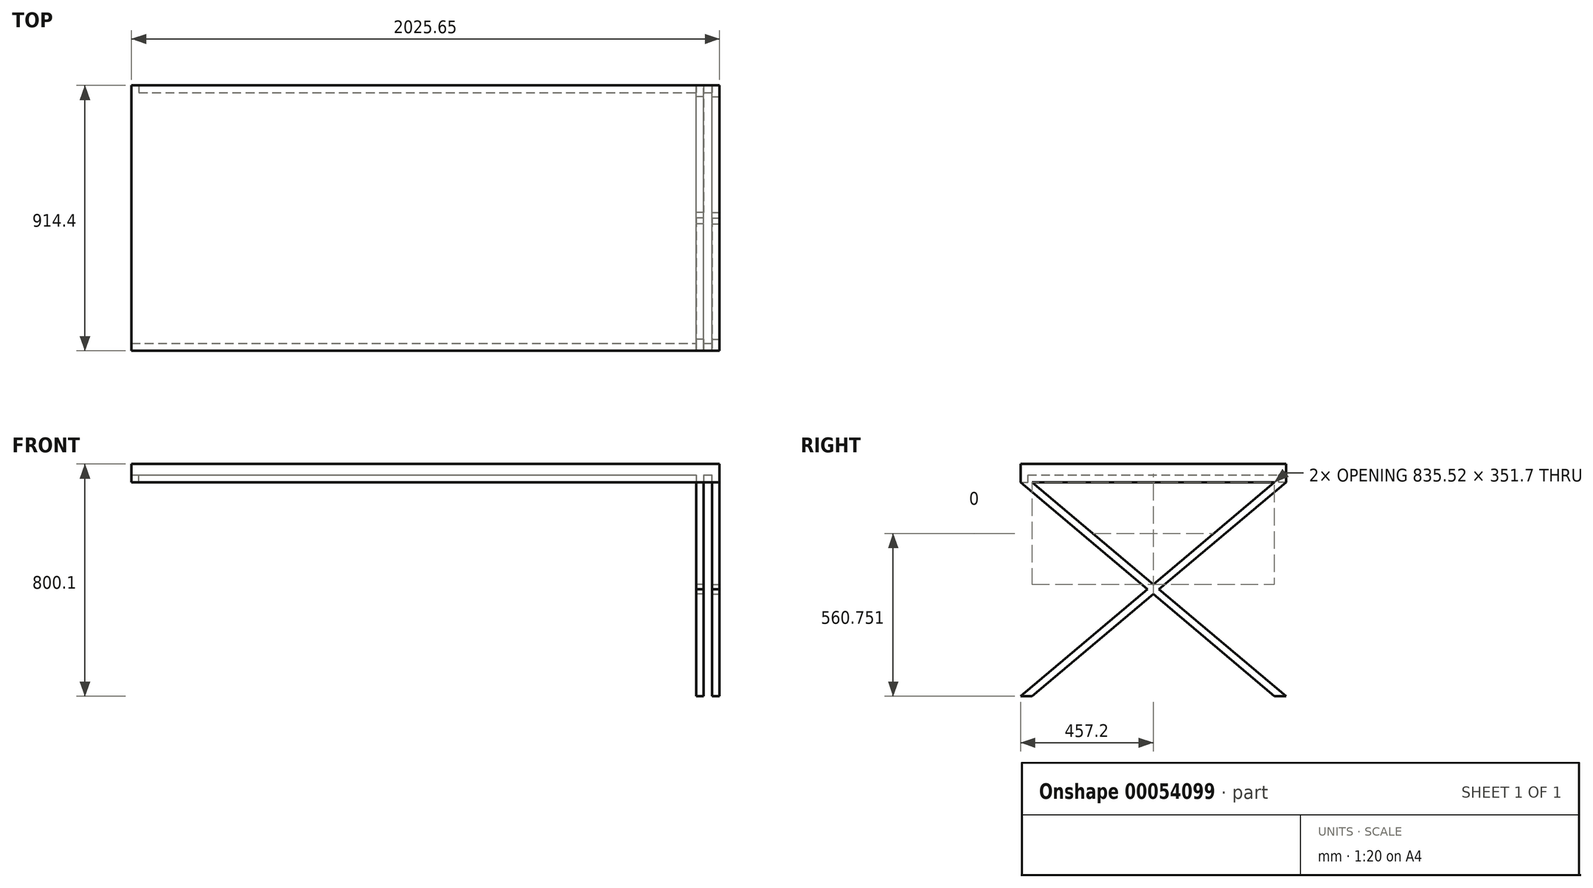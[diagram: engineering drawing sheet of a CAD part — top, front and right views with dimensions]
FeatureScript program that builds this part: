
annotation { "Feature Type Name" : "Feature", "Feature Type Description" : "" }
export const myFeature = defineFeature(function(context is Context, id is Id, definition is map)
    precondition{}
    {
        {
            var Q0;
            Q0=qCreatedBy(makeId("Right.planeOp"),FACE);
            var sketch = newSketch(context, id + "F0", { "sketchPlane" : qUnion([Q0])});
            skLineSegment(sketch, "E0.rect.bottom", {"start": v(-457.2, 368.3) * mm, "end": v(457.2, 368.3) * mm, "construction": true});
            skLineSegment(sketch, "E0.rect.top", {"start": v(-457.2, -368.3) * mm, "end": v(457.2, -368.3) * mm, "construction": true});
            skLineSegment(sketch, "E0.rect.left", {"start": v(-457.2, 368.3) * mm, "end": v(-457.2, -368.3) * mm, "construction": true});
            skLineSegment(sketch, "E0.rect.right", {"start": v(457.2, 368.3) * mm, "end": v(457.2, -368.3) * mm, "construction": true});
            skPoint(sketch, "E0.rect.middle", {"position": v(0, 0) * mm});
            skLineSegment(sketch, "E1", {"start": v(-457.2, 368.3) * mm, "end": v(417.76, -368.3) * mm});
            skLineSegment(sketch, "E2", {"start": v(417.76, -368.3) * mm, "end": v(457.2, -368.3) * mm});
            skLineSegment(sketch, "E3", {"start": v(457.2, -368.3) * mm, "end": v(-417.76, 368.3) * mm});
            skLineSegment(sketch, "E4", {"start": v(-417.76, 368.3) * mm, "end": v(-457.2, 368.3) * mm});
            skLineSegment(sketch, "E5", {"start": v(417.76, 368.3) * mm, "end": v(457.2, 368.3) * mm});
            skLineSegment(sketch, "E6", {"start": v(-417.76, -368.3) * mm, "end": v(457.2, 368.3) * mm});
            skLineSegment(sketch, "E7", {"start": v(-417.76, -368.3) * mm, "end": v(-457.2, -368.3) * mm});
            skLineSegment(sketch, "E8", {"start": v(-457.2, -368.3) * mm, "end": v(417.76, 368.3) * mm});
            skLineSegment(sketch, "E9.bottom", {"start": v(-457.2, 368.3) * mm, "end": v(457.2, 368.3) * mm});
            skLineSegment(sketch, "E9.top", {"start": v(-457.2, 393.7) * mm, "end": v(457.2, 393.7) * mm});
            skLineSegment(sketch, "E9.left", {"start": v(-457.2, 368.3) * mm, "end": v(-457.2, 393.7) * mm});
            skLineSegment(sketch, "E9.right", {"start": v(457.2, 368.3) * mm, "end": v(457.2, 393.7) * mm});
            skSolve(sketch);
        }
        {
            var Q0;
            Q0 = qSketchRegion(id + "F0", true);
            extrude(context, id + "F1", {"entities" : qUnion([Q0]), "oppositeDirection" : true, "depth" : 25.4 * mm});
        }
        {
            var Q0;
            Q0=qCreatedBy(makeId("Right.planeOp"),FACE);
            cPlane(context, id + "F2", {"entities" : qUnion([Q0]), "cplaneType" : CPlaneType.OFFSET, "offset" : (79 + (3 / 4)) * mm, "oppositeDirection" : true, "width" : 152.4 * mm, "height" : 152.4 * mm});
        }
        {
            var Q0;
            Q0=qCreatedBy(id+"F2.planeOp",FACE);
            var sketch = newSketch(context, id + "F3", { "sketchPlane" : qUnion([Q0])});
            skLineSegment(sketch, "E10.rect.bottom", {"start": v(-457.2, 368.3) * mm, "end": v(457.2, 368.3) * mm, "construction": true});
            skLineSegment(sketch, "E10.rect.top", {"start": v(-457.2, -368.3) * mm, "end": v(457.2, -368.3) * mm, "construction": true});
            skLineSegment(sketch, "E10.rect.left", {"start": v(-457.2, 368.3) * mm, "end": v(-457.2, -368.3) * mm, "construction": true});
            skLineSegment(sketch, "E10.rect.right", {"start": v(457.2, 368.3) * mm, "end": v(457.2, -368.3) * mm, "construction": true});
            skPoint(sketch, "E10.rect.middle", {"position": v(0, 0) * mm});
            skLineSegment(sketch, "E11", {"start": v(-457.2, 368.3) * mm, "end": v(417.76, -368.3) * mm});
            skLineSegment(sketch, "E12", {"start": v(417.76, -368.3) * mm, "end": v(457.2, -368.3) * mm});
            skLineSegment(sketch, "E13", {"start": v(457.2, -368.3) * mm, "end": v(-417.76, 368.3) * mm});
            skLineSegment(sketch, "E14", {"start": v(-417.76, 368.3) * mm, "end": v(-457.2, 368.3) * mm});
            skLineSegment(sketch, "E15", {"start": v(417.76, 368.3) * mm, "end": v(457.2, 368.3) * mm});
            skLineSegment(sketch, "E16", {"start": v(-417.76, -368.3) * mm, "end": v(457.2, 368.3) * mm});
            skLineSegment(sketch, "E17", {"start": v(-417.76, -368.3) * mm, "end": v(-457.2, -368.3) * mm});
            skLineSegment(sketch, "E18", {"start": v(-457.2, -368.3) * mm, "end": v(417.76, 368.3) * mm});
            skLineSegment(sketch, "E19.bottom", {"start": v(-457.2, 368.3) * mm, "end": v(457.2, 368.3) * mm});
            skLineSegment(sketch, "E19.top", {"start": v(-457.2, 393.7) * mm, "end": v(457.2, 393.7) * mm});
            skLineSegment(sketch, "E19.left", {"start": v(-457.2, 368.3) * mm, "end": v(-457.2, 393.7) * mm});
            skLineSegment(sketch, "E19.right", {"start": v(457.2, 368.3) * mm, "end": v(457.2, 393.7) * mm});
            skSolve(sketch);
        }
        {
            var Q0;
            Q0 = qSketchRegion(id + "F3", true);
            extrude(context, id + "F4", {"entities" : qUnion([Q0]), "depth" : 25.4 * mm});
        }
        {
            var Q0;
            Q0=makeQuery(id+"F4.opExtrude","SWEPT_FACE",FACE,{"disambiguationData":[OSD([sQuery(id+"F3.wireOp",EDGE,"E19.top")])]});
            var sketch = newSketch(context, id + "F5", { "sketchPlane" : qUnion([Q0])});
            skLineSegment(sketch, "E20.bottom", {"start": v(-2025.65, -457.2) * mm, "end": v(0, -457.2) * mm});
            skLineSegment(sketch, "E20.top", {"start": v(-2025.65, 457.2) * mm, "end": v(0, 457.2) * mm});
            skLineSegment(sketch, "E20.left", {"start": v(-2025.65, -457.2) * mm, "end": v(-2025.65, 457.2) * mm});
            skLineSegment(sketch, "E20.right", {"start": v(0, -457.2) * mm, "end": v(0, 457.2) * mm});
            skSolve(sketch);
        }
        {
            var Q0;
            Q0 = qSketchRegion(id + "F5", true);
            extrude(context, id + "F6", {"entities" : qUnion([Q0]), "depth" : 38.1 * mm});
        }
        {
            var Q0;
            Q0=makeQuery(id+"F4.opExtrude","SWEPT_FACE",FACE,{"disambiguationData":[OSD([sQuery(id+"F3.wireOp",EDGE,"E19.top")])]});
            var sketch = newSketch(context, id + "F7", { "sketchPlane" : qUnion([Q0])});
            skLineSegment(sketch, "E21.bottom", {"start": v(-2000.25, 457.2) * mm, "end": v(-25.4, 457.2) * mm});
            skLineSegment(sketch, "E21.top", {"start": v(-2000.25, 431.8) * mm, "end": v(-25.4, 431.8) * mm});
            skLineSegment(sketch, "E21.left", {"start": v(-2000.25, 457.2) * mm, "end": v(-2000.25, 431.8) * mm});
            skLineSegment(sketch, "E21.right", {"start": v(-25.4, 457.2) * mm, "end": v(-25.4, 431.8) * mm});
            skLineSegment(sketch, "E22.bottom", {"start": v(-2025.65, -457.2) * mm, "end": v(-25.4, -457.2) * mm});
            skLineSegment(sketch, "E22.top", {"start": v(-2025.65, -431.8) * mm, "end": v(-25.4, -431.8) * mm});
            skLineSegment(sketch, "E22.left", {"start": v(-2025.65, -457.2) * mm, "end": v(-2025.65, -431.8) * mm});
            skLineSegment(sketch, "E22.right", {"start": v(-25.4, -457.2) * mm, "end": v(-25.4, -431.8) * mm});
            skSolve(sketch);
        }
        {
            var Q0;
            Q0 = qSketchRegion(id + "F7", true);
            extrude(context, id + "F8", {"entities" : qUnion([Q0]), "operationType" : NewBodyOperationType.ADD, "oppositeDirection" : true, "depth" : 25.4 * mm});
        }
    });
